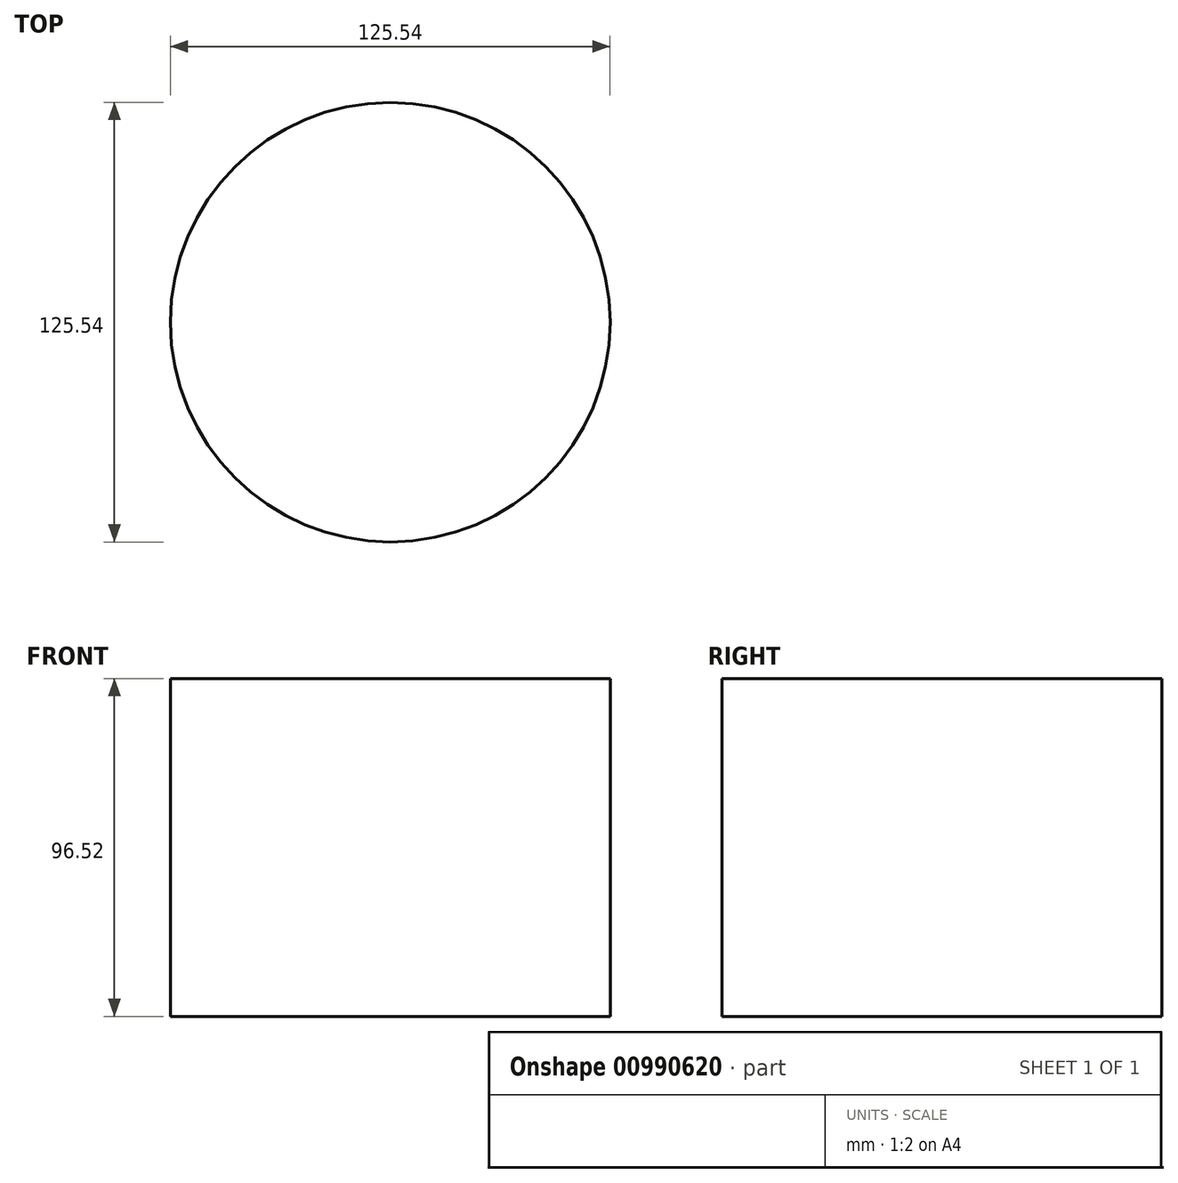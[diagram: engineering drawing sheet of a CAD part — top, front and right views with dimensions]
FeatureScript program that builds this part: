
annotation { "Feature Type Name" : "Feature", "Feature Type Description" : "" }
export const myFeature = defineFeature(function(context is Context, id is Id, definition is map)
    precondition{}
    {
        {
            var Q0;
            Q0=qCreatedBy(makeId("Top.planeOp"),FACE);
            var sketch = newSketch(context, id + "F0", { "sketchPlane" : qUnion([Q0])});
            skCircle(sketch, "E0", {"center": v(0, 0) * mm, "radius": 62.77 * mm});
            skSolve(sketch);
        }
        {
            var Q0;
            Q0=makeQuery(id+"F0.imprint","IMPRINT",FACE,{"disambiguationData":[TD([[makeQuery(id+"F0.imprint","IMPRINT",EDGE,{"derivedFrom":sQuery(id+"F0.wireOp",EDGE,"E0")}),1.0]])]});
            extrude(context, id + "F1", {"entities" : qUnion([Q0]), "depth" : 96.52 * mm, "offsetDistance" : 25.4 * mm});
        }
    });
